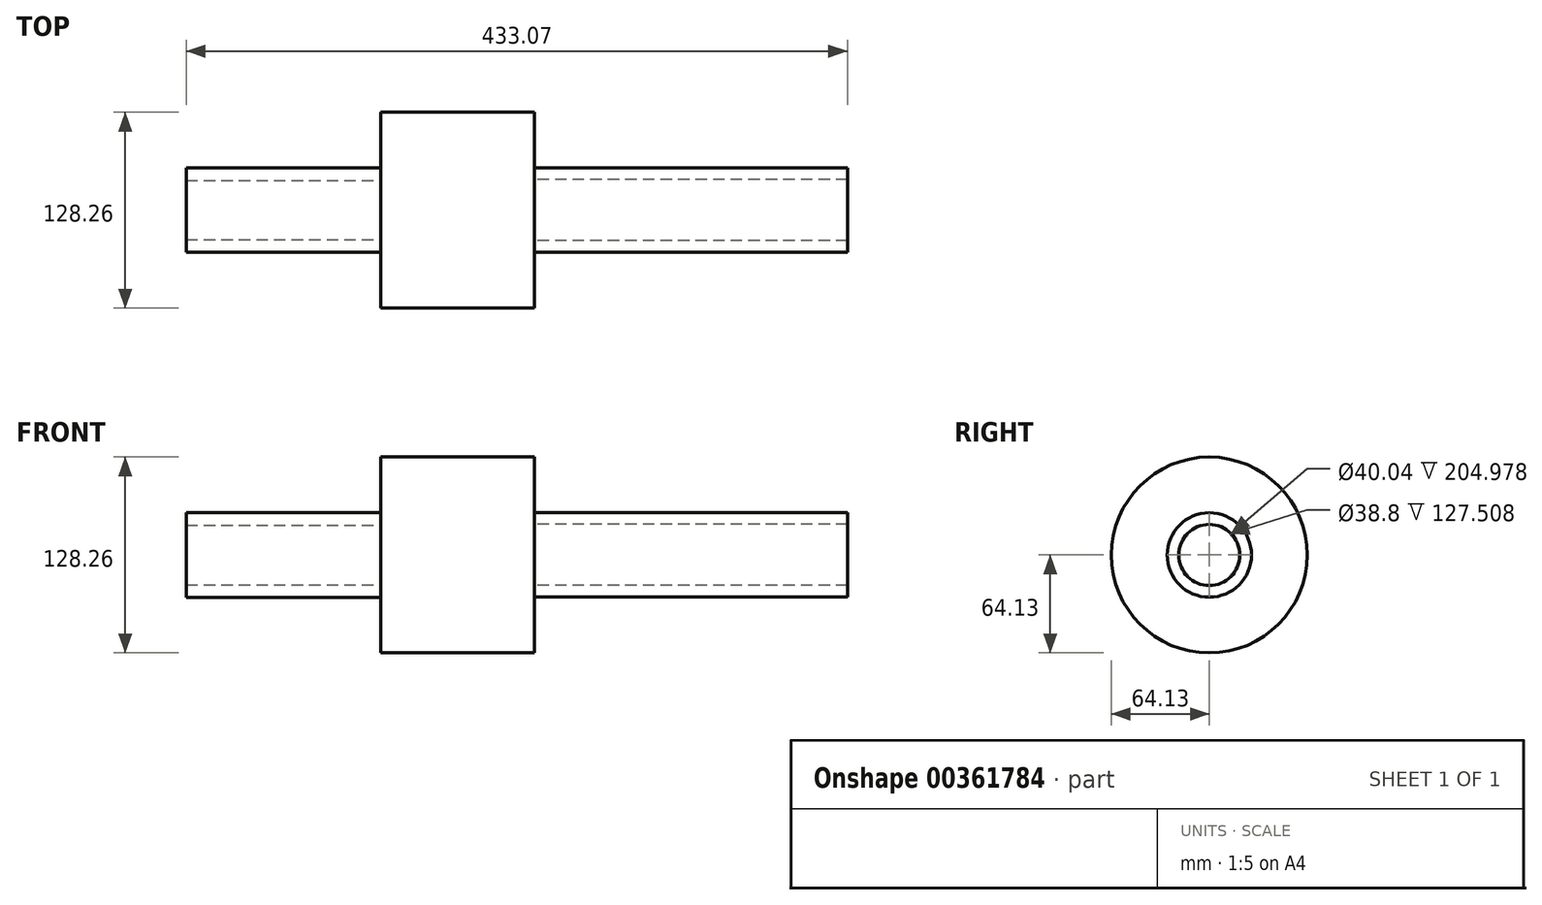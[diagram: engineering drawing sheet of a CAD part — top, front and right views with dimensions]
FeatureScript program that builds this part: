
annotation { "Feature Type Name" : "Feature", "Feature Type Description" : "" }
export const myFeature = defineFeature(function(context is Context, id is Id, definition is map)
    precondition{}
    {
        {
            var Q0;
            Q0=qCreatedBy(makeId("Right.planeOp"),FACE);
            var sketch = newSketch(context, id + "F0", { "sketchPlane" : qUnion([Q0])});
            skCircle(sketch, "E0", {"center": v(0, 0) * mm, "radius": 64.13 * mm});
            skSolve(sketch);
        }
        {
            var Q0;
            Q0 = qSketchRegion(id + "F0", true);
            extrude(context, id + "F1", {"entities" : qUnion([Q0]), "depth" : 100.58 * mm});
        }
        {
            var Q0;
            Q0=makeQuery(id+"F1.opExtrude","CAP_FACE",FACE,{"disambiguationData":[OSD([sQuery(id+"F0.wireOp",EDGE,"E0")])],"isStart":false});
            var sketch = newSketch(context, id + "F2", { "sketchPlane" : qUnion([Q0])});
            skCircle(sketch, "E1", {"center": v(0, 0) * mm, "radius": 20.02 * mm});
            skCircle(sketch, "E2", {"center": v(0, 0) * mm, "radius": 27.6 * mm});
            skSolve(sketch);
        }
        {
            var Q0;
            Q0 = qSketchRegion(id + "F2", true);
            extrude(context, id + "F3", {"entities" : qUnion([Q0]), "operationType" : NewBodyOperationType.ADD, "depth" : 204.98 * mm});
        }
        {
            var Q0;
            Q0=makeQuery(id+"F1.opExtrude","CAP_FACE",FACE,{"disambiguationData":[OSD([sQuery(id+"F0.wireOp",EDGE,"E0")])],"isStart":true});
            var sketch = newSketch(context, id + "F4", { "sketchPlane" : qUnion([Q0])});
            skCircle(sketch, "E3", {"center": v(0, 0) * mm, "radius": 19.4 * mm});
            skCircle(sketch, "E4", {"center": v(0, 0) * mm, "radius": 27.65 * mm});
            skSolve(sketch);
        }
        {
            var Q0;
            Q0 = qSketchRegion(id + "F4", true);
            extrude(context, id + "F5", {"entities" : qUnion([Q0]), "operationType" : NewBodyOperationType.ADD, "depth" : 127.5 * mm});
        }
    });
